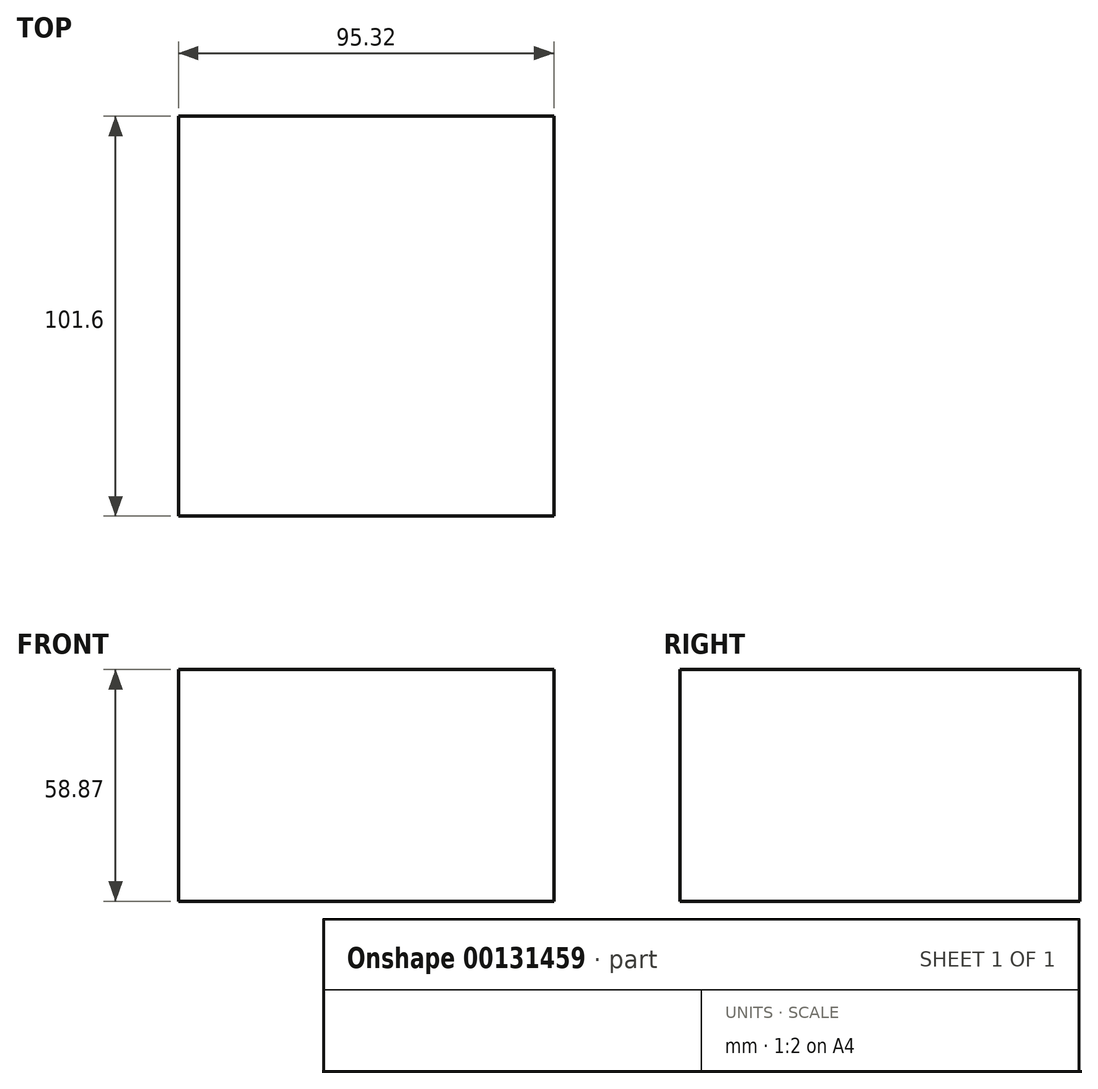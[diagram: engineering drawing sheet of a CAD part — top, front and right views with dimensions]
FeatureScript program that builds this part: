
annotation { "Feature Type Name" : "Feature", "Feature Type Description" : "" }
export const myFeature = defineFeature(function(context is Context, id is Id, definition is map)
    precondition{}
    {
        {
            var Q0;
            Q0=qCreatedBy(makeId("Front.planeOp"),FACE);
            var sketch = newSketch(context, id + "F0", { "sketchPlane" : qUnion([Q0])});
            skLineSegment(sketch, "E0.bottom", {"start": v(-52.47, 27.54) * mm, "end": v(42.85, 27.54) * mm});
            skLineSegment(sketch, "E0.top", {"start": v(-52.47, -31.33) * mm, "end": v(42.85, -31.33) * mm});
            skLineSegment(sketch, "E0.left", {"start": v(-52.47, 27.54) * mm, "end": v(-52.47, -31.33) * mm});
            skLineSegment(sketch, "E0.right", {"start": v(42.85, 27.54) * mm, "end": v(42.85, -31.33) * mm});
            skSolve(sketch);
        }
        {
            var Q0;
            Q0=makeQuery(id+"F0.imprint","IMPRINT",FACE,{"disambiguationData":[TD([[makeQuery(id+"F0.imprint","IMPRINT",EDGE,{"derivedFrom":sQuery(id+"F0.wireOp",EDGE,"E0.bottom")}),-1.0]])]});
            extrude(context, id + "F1", {"entities" : qUnion([Q0]), "depth" : 101.6 * mm});
        }
    });
